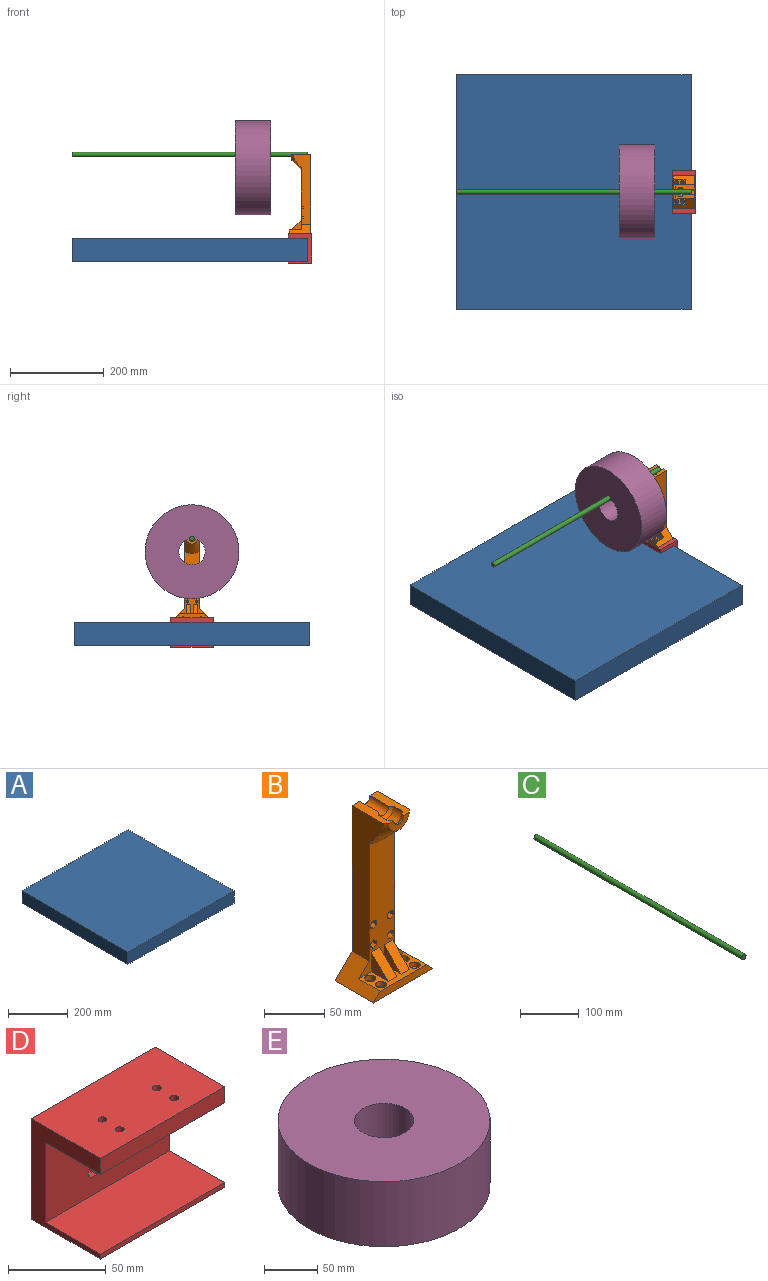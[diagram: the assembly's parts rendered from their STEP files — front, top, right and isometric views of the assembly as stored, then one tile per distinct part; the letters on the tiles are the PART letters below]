
ASSEMBLY  parts=5 mates=4
PART A: 6 faces, bbox 500x500x50 mm
  f0: plane 500x50mm, normal (0,-1,0), area 25000mm2, adj f1,f3,f4,f5
  f1: plane 500x50mm, normal (1,0,0), area 25000mm2, adj f0,f2,f4,f5
  f2: plane 500x50mm, normal (0,1,0), area 25000mm2, adj f1,f3,f4,f5
  f3: plane 500x50mm, normal (-1,0,0), area 25000mm2, adj f0,f2,f4,f5
  f4: plane 500x500mm, normal (0,0,1), area 250000mm2, adj f0,f1,f2,f3
  f5: plane 500x500mm, normal (0,0,-1), area 250000mm2, adj f0,f1,f2,f3
PART B: 68 faces, bbox 70x45x168 mm
  f0: plane 70x45mm, normal (0,0,-1), area 3085.5mm2, adj f11,f14,f17,f20,f64,f65,f66,f67
  f1: cone r=9mm half-angle=45deg, axis (0,-1,0), area 100mm2, adj f2,f53,f54,f55
  f2: cylinder r=9mm len=18mm, axis (0,1,0), area 282.7mm2, adj f1,f3,f53,f55
  f3: cone r=9mm half-angle=45deg, axis (0,1,0), area 100mm2, adj f2,f4,f53,f55
  f4: cylinder r=6mm len=12mm, axis (0,-1,0), area 37.7mm2, adj f3,f5,f53,f55
  f5: plane 24x12mm, normal (0,-1,0), area 169.6mm2, adj f4,f52,f53,f55
  f6: plane 8.33x7.21mm, normal (0,-1,0), area 28.9mm2, adj f22,f23,f24,f25,f26,f27,f56
  f7: plane 8.33x7.21mm, normal (0,-1,0), area 28.9mm2, adj f28,f29,f30,f31,f32,f33,f57
  f8: plane 8.33x7.21mm, normal (0,-1,0), area 28.9mm2, adj f34,f35,f36,f37,f38,f39,f58
  f9: plane 8.33x7.21mm, normal (0,-1,0), area 28.9mm2, adj f40,f41,f42,f43,f44,f45,f59
  f10: plane 9x9mm, normal (0,0,1), area 47.5mm2, adj f11,f12
  f11: cylinder r=2.27mm len=4.53mm, axis (0,0,-1), area 42.7mm2, adj f0,f10
  f12: cylinder r=4.5mm len=9mm, axis (0,0,1), area 141.4mm2, adj f10,f61
  f13: plane 9x9mm, normal (0,0,1), area 47.5mm2, adj f14,f15
  f14: cylinder r=2.27mm len=4.53mm, axis (0,0,-1), area 42.7mm2, adj f0,f13
  f15: cylinder r=4.5mm len=9mm, axis (0,0,1), area 141.4mm2, adj f13,f61
  f16: plane 9x9mm, normal (0,0,1), area 47.5mm2, adj f17,f18
  f17: cylinder r=2.27mm len=4.53mm, axis (0,0,-1), area 42.7mm2, adj f0,f16
  f18: cylinder r=4.5mm len=9mm, axis (0,0,1), area 141.4mm2, adj f16,f61
  f19: plane 9x9mm, normal (0,0,1), area 47.5mm2, adj f20,f21
  f20: cylinder r=2.27mm len=4.53mm, axis (0,0,-1), area 42.7mm2, adj f0,f19
  f21: cylinder r=4.5mm len=9mm, axis (0,0,1), area 141.4mm2, adj f19,f61
  f22: plane 4.8x3.61mm, normal (0.5,0,-0.87), area 20mm2, adj f6,f23,f27,f62
  f23: plane 4.8x4.16mm, normal (1,0,0), area 20mm2, adj f6,f22,f24,f62
  f24: plane 4.8x3.61mm, normal (0.5,0,0.87), area 20mm2, adj f6,f23,f25,f62
  f25: plane 4.8x3.61mm, normal (-0.5,0,0.87), area 20mm2, adj f6,f24,f26,f62
  f26: plane 4.8x4.16mm, normal (-1,0,0), area 20mm2, adj f6,f25,f27,f62
  f27: plane 4.8x3.61mm, normal (-0.5,0,-0.87), area 20mm2, adj f6,f22,f26,f62
  f28: plane 4.8x3.61mm, normal (0.5,0,-0.87), area 20mm2, adj f7,f29,f33,f62
  f29: plane 4.8x4.16mm, normal (1,0,0), area 20mm2, adj f7,f28,f30,f62
  f30: plane 4.8x3.61mm, normal (0.5,0,0.87), area 20mm2, adj f7,f29,f31,f62
  f31: plane 4.8x3.61mm, normal (-0.5,0,0.87), area 20mm2, adj f7,f30,f32,f62
  f32: plane 4.8x4.16mm, normal (-1,0,0), area 20mm2, adj f7,f31,f33,f62
  f33: plane 4.8x3.61mm, normal (-0.5,0,-0.87), area 20mm2, adj f7,f28,f32,f62
  f34: plane 4.8x3.61mm, normal (0.5,0,-0.87), area 20mm2, adj f8,f35,f39,f62
  f35: plane 4.8x4.16mm, normal (1,0,0), area 20mm2, adj f8,f34,f36,f62
  f36: plane 4.8x3.61mm, normal (0.5,0,0.87), area 20mm2, adj f8,f35,f37,f62
  f37: plane 4.8x3.61mm, normal (-0.5,0,0.87), area 20mm2, adj f8,f36,f38,f62
  f38: plane 4.8x4.16mm, normal (-1,0,0), area 20mm2, adj f8,f37,f39,f62
  f39: plane 4.8x3.61mm, normal (-0.5,0,-0.87), area 20mm2, adj f8,f34,f38,f62
  f40: plane 4.8x3.61mm, normal (0.5,0,-0.87), area 20mm2, adj f9,f41,f45,f62
  f41: plane 4.8x4.16mm, normal (1,0,0), area 20mm2, adj f9,f40,f42,f62
  f42: plane 4.8x3.61mm, normal (0.5,0,0.87), area 20mm2, adj f9,f41,f43,f62
  f43: plane 4.8x3.61mm, normal (-0.5,0,0.87), area 20mm2, adj f9,f42,f44,f62
  f44: plane 4.8x4.16mm, normal (-1,0,0), area 20mm2, adj f9,f43,f45,f62
  f45: plane 4.8x3.61mm, normal (-0.5,0,-0.87), area 20mm2, adj f9,f40,f44,f62
  f46: plane 20x20mm, normal (1,0,0), area 200mm2, adj f47,f61,f62
  f47: plane 20x20mm, normal (0,-0.71,0.71), area 282.8mm2, adj f46,f48,f61,f62
  f48: plane 20x20mm, normal (-1,0,0), area 200mm2, adj f47,f61,f62
  f49: plane 20x20mm, normal (1,0,0), area 200mm2, adj f50,f61,f62
  f50: plane 20x20mm, normal (0,-0.71,0.71), area 282.8mm2, adj f49,f51,f61,f62
  f51: plane 20x20mm, normal (-1,0,0), area 200mm2, adj f50,f61,f62
  f52: cone r=12mm half-angle=45deg, axis (0,1,0), area 986.3mm2, adj f5,f53,f55,f60,f62,f63
  f53: plane 40x9mm, normal (0,0,1), area 316.5mm2, adj f1,f2,f3,f4,f5,f52,f54,f63
  f54: cylinder r=6mm len=22mm, axis (0,-1,0), area 414.7mm2, adj f1,f53,f55,f67
  f55: plane 40x9mm, normal (0,0,1), area 316.5mm2, adj f1,f2,f3,f4,f5,f52,f54,f60
  f56: cylinder r=2.27mm len=15.2mm, axis (0,-1,0), area 216.4mm2, adj f6,f67
  f57: cylinder r=2.27mm len=15.2mm, axis (0,-1,0), area 216.4mm2, adj f7,f67
  f58: cylinder r=2.27mm len=15.2mm, axis (0,-1,0), area 216.4mm2, adj f8,f67
  f59: cylinder r=2.27mm len=15.2mm, axis (0,-1,0), area 216.4mm2, adj f9,f67
  f60: plane 148.01x37.01mm, normal (-1,0,0), area 3255.8mm2, adj f52,f55,f62,f64,f67
  f61: plane 54x25mm, normal (0,0,1), area 695.5mm2, adj f12,f15,f18,f21,f46,f47,f48,f49
  f62: plane 131.73x54mm, normal (0,-1,0), area 3440.3mm2, adj f22,f23,f24,f25,f26,f27,f28,f29
  f63: plane 148.01x37.01mm, normal (1,0,0), area 3255.8mm2, adj f52,f53,f62,f65,f67
  f64: plane 45x20mm, normal (-0.71,0,0.71), area 848.5mm2, adj f0,f60,f61,f62,f66,f67
  f65: plane 45x20mm, normal (0.71,0,0.71), area 848.5mm2, adj f0,f61,f62,f63,f66,f67
  f66: plane 70x8mm, normal (0,-1,0), area 496mm2, adj f0,f61,f64,f65
  f67: plane 168x70mm, normal (0,1,0), area 5318.9mm2, adj f0,f53,f54,f55,f56,f57,f58,f59
PART C: 3 faces, bbox 10x500x10 mm
  f0: cylinder r=5mm len=500mm, axis (0,1,0), area 15708mm2, adj f1,f2
  f1: plane 10x10mm, normal (0,-1,0), area 78.5mm2, adj f0
  f2: plane 10x10mm, normal (0,1,0), area 78.5mm2, adj f0
PART D: 78 faces, bbox 90x50x63.1 mm
  f0: cylinder r=2.27mm len=4.8mm, axis (0,0,-1), area 68.3mm2, adj f8,f67
  f1: cylinder r=2.27mm len=4.8mm, axis (0,0,-1), area 68.3mm2, adj f8,f60
  f2: cylinder r=2.27mm len=4.8mm, axis (0,0,-1), area 68.3mm2, adj f8,f53
  f3: cylinder r=2.27mm len=4.8mm, axis (0,0,-1), area 68.3mm2, adj f8,f46
  f4: cylinder r=2.27mm len=4.53mm, axis (0,-1,0), area 45.6mm2, adj f39,f75
  f5: cylinder r=2.27mm len=4.53mm, axis (0,-1,0), area 45.6mm2, adj f32,f74
  f6: cylinder r=2.27mm len=4.53mm, axis (0,-1,0), area 45.6mm2, adj f25,f77
  f7: cylinder r=2.27mm len=4.53mm, axis (0,-1,0), area 45.6mm2, adj f18,f76
  f8: plane 90x50mm, normal (0,0,1), area 4435.5mm2, adj f0,f1,f2,f3,f10,f12,f13,f15
  f9: plane 90x50.1mm, normal (0,-1,0), area 4328.9mm2, adj f10,f12,f14,f16,f19,f20,f21,f22
  f10: plane 63.1x50mm, normal (-1,0,0), area 1151mm2, adj f8,f9,f11,f13,f14,f15,f16,f17
  f11: plane 90x50mm, normal (0,0,-1), area 4500mm2, adj f10,f12,f13,f17
  f12: plane 63.1x50mm, normal (1,0,0), area 1151mm2, adj f8,f9,f11,f13,f14,f15,f16,f17
  f13: plane 90x63.1mm, normal (0,1,0), area 5450.3mm2, adj f8,f10,f11,f12,f74,f75,f76,f77
  f14: plane 90x40mm, normal (0,0,-1), area 3419.9mm2, adj f9,f10,f12,f15,f47,f48,f49,f50
  f15: plane 90x10mm, normal (0,-1,0), area 900mm2, adj f8,f10,f12,f14
  f16: plane 90x40mm, normal (0,0,1), area 3600mm2, adj f9,f10,f12,f17
  f17: plane 90x3mm, normal (0,-1,0), area 270mm2, adj f10,f11,f12,f16
  f18: plane 8.33x7.21mm, normal (0,-1,0), area 28.9mm2, adj f7,f19,f20,f21,f22,f23,f24
  f19: plane 4.8x3.61mm, normal (-0.87,0,0.5), area 20mm2, adj f9,f18,f20,f24
  f20: plane 4.8x3.61mm, normal (-0.87,0,-0.5), area 20mm2, adj f9,f18,f19,f21
  f21: plane 4.8x4.16mm, normal (0,0,-1), area 20mm2, adj f9,f18,f20,f22
  f22: plane 4.8x3.61mm, normal (0.87,0,-0.5), area 20mm2, adj f9,f18,f21,f23
  f23: plane 4.8x3.61mm, normal (0.87,0,0.5), area 20mm2, adj f9,f18,f22,f24
  f24: plane 4.8x4.16mm, normal (0,0,1), area 20mm2, adj f9,f18,f19,f23
  f25: plane 8.33x7.21mm, normal (0,-1,0), area 28.9mm2, adj f6,f26,f27,f28,f29,f30,f31
  f26: plane 4.8x3.61mm, normal (-0.87,0,0.5), area 20mm2, adj f9,f25,f27,f31
  f27: plane 4.8x3.61mm, normal (-0.87,0,-0.5), area 20mm2, adj f9,f25,f26,f28
  f28: plane 4.8x4.16mm, normal (0,0,-1), area 20mm2, adj f9,f25,f27,f29
  f29: plane 4.8x3.61mm, normal (0.87,0,-0.5), area 20mm2, adj f9,f25,f28,f30
  f30: plane 4.8x3.61mm, normal (0.87,0,0.5), area 20mm2, adj f9,f25,f29,f31
  f31: plane 4.8x4.16mm, normal (0,0,1), area 20mm2, adj f9,f25,f26,f30
  f32: plane 8.33x7.21mm, normal (0,-1,0), area 28.9mm2, adj f5,f33,f34,f35,f36,f37,f38
  f33: plane 4.8x3.61mm, normal (-0.87,0,0.5), area 20mm2, adj f9,f32,f34,f38
  f34: plane 4.8x3.61mm, normal (-0.87,0,-0.5), area 20mm2, adj f9,f32,f33,f35
  f35: plane 4.8x4.16mm, normal (0,0,-1), area 20mm2, adj f9,f32,f34,f36
  f36: plane 4.8x3.61mm, normal (0.87,0,-0.5), area 20mm2, adj f9,f32,f35,f37
  f37: plane 4.8x3.61mm, normal (0.87,0,0.5), area 20mm2, adj f9,f32,f36,f38
  f38: plane 4.8x4.16mm, normal (0,0,1), area 20mm2, adj f9,f32,f33,f37
  f39: plane 8.33x7.21mm, normal (0,-1,0), area 28.9mm2, adj f4,f40,f41,f42,f43,f44,f45
  f40: plane 4.8x3.61mm, normal (-0.87,0,0.5), area 20mm2, adj f9,f39,f41,f45
  f41: plane 4.8x3.61mm, normal (-0.87,0,-0.5), area 20mm2, adj f9,f39,f40,f42
  f42: plane 4.8x4.16mm, normal (0,0,-1), area 20mm2, adj f9,f39,f41,f43
  f43: plane 4.8x3.61mm, normal (0.87,0,-0.5), area 20mm2, adj f9,f39,f42,f44
  f44: plane 4.8x3.61mm, normal (0.87,0,0.5), area 20mm2, adj f9,f39,f43,f45
  f45: plane 4.8x4.16mm, normal (0,0,1), area 20mm2, adj f9,f39,f40,f44
  f46: plane 8.33x7.21mm, normal (0,0,-1), area 28.9mm2, adj f3,f47,f48,f49,f50,f51,f52
  f47: plane 5.2x3.61mm, normal (-0.87,-0.5,0), area 21.6mm2, adj f14,f46,f48,f52
  f48: plane 5.2x3.61mm, normal (-0.87,0.5,0), area 21.6mm2, adj f14,f46,f47,f49
  f49: plane 5.2x4.16mm, normal (0,1,0), area 21.6mm2, adj f14,f46,f48,f50
  f50: plane 5.2x3.61mm, normal (0.87,0.5,0), area 21.6mm2, adj f14,f46,f49,f51
  f51: plane 5.2x3.61mm, normal (0.87,-0.5,0), area 21.6mm2, adj f14,f46,f50,f52
  f52: plane 5.2x4.16mm, normal (0,-1,0), area 21.6mm2, adj f14,f46,f47,f51
  f53: plane 8.33x7.21mm, normal (0,0,-1), area 28.9mm2, adj f2,f54,f55,f56,f57,f58,f59
  f54: plane 5.2x3.61mm, normal (-0.87,-0.5,0), area 21.6mm2, adj f14,f53,f55,f59
  f55: plane 5.2x3.61mm, normal (-0.87,0.5,0), area 21.6mm2, adj f14,f53,f54,f56
  f56: plane 5.2x4.16mm, normal (0,1,0), area 21.6mm2, adj f14,f53,f55,f57
  f57: plane 5.2x3.61mm, normal (0.87,0.5,0), area 21.6mm2, adj f14,f53,f56,f58
  f58: plane 5.2x3.61mm, normal (0.87,-0.5,0), area 21.6mm2, adj f14,f53,f57,f59
  f59: plane 5.2x4.16mm, normal (0,-1,0), area 21.6mm2, adj f14,f53,f54,f58
  f60: plane 8.33x7.21mm, normal (0,0,-1), area 28.9mm2, adj f1,f61,f62,f63,f64,f65,f66
  f61: plane 5.2x3.61mm, normal (-0.87,-0.5,0), area 21.6mm2, adj f14,f60,f62,f66
  f62: plane 5.2x3.61mm, normal (-0.87,0.5,0), area 21.6mm2, adj f14,f60,f61,f63
  f63: plane 5.2x4.16mm, normal (0,1,0), area 21.6mm2, adj f14,f60,f62,f64
  f64: plane 5.2x3.61mm, normal (0.87,0.5,0), area 21.6mm2, adj f14,f60,f63,f65
  f65: plane 5.2x3.61mm, normal (0.87,-0.5,0), area 21.6mm2, adj f14,f60,f64,f66
  f66: plane 5.2x4.16mm, normal (0,-1,0), area 21.6mm2, adj f14,f60,f61,f65
  f67: plane 8.33x7.21mm, normal (0,0,-1), area 28.9mm2, adj f0,f68,f69,f70,f71,f72,f73
  f68: plane 5.2x3.61mm, normal (-0.87,-0.5,0), area 21.6mm2, adj f14,f67,f69,f73
  f69: plane 5.2x3.61mm, normal (-0.87,0.5,0), area 21.6mm2, adj f14,f67,f68,f70
  f70: plane 5.2x4.16mm, normal (0,1,0), area 21.6mm2, adj f14,f67,f69,f71
  f71: plane 5.2x3.61mm, normal (0.87,0.5,0), area 21.6mm2, adj f14,f67,f70,f72
  f72: plane 5.2x3.61mm, normal (0.87,-0.5,0), area 21.6mm2, adj f14,f67,f71,f73
  f73: plane 5.2x4.16mm, normal (0,-1,0), area 21.6mm2, adj f14,f67,f68,f72
  f74: cone r=4.27mm half-angle=45deg, axis (0,1,0), area 58mm2, adj f5,f13
  f75: cone r=4.27mm half-angle=45deg, axis (0,1,0), area 58mm2, adj f4,f13
  f76: cone r=4.27mm half-angle=45deg, axis (0,1,0), area 58mm2, adj f7,f13
  f77: cone r=4.27mm half-angle=45deg, axis (0,1,0), area 58mm2, adj f6,f13
PART E: 4 faces, bbox 200x200x75 mm
  f0: cylinder r=28mm len=75mm, axis (0,0,-1), area 13194.7mm2, adj f2,f3
  f1: cylinder r=100mm len=200mm, axis (0,0,-1), area 47123.9mm2, adj f2,f3
  f2: plane 200x200mm, normal (0,0,1), area 28952.9mm2, adj f0,f1
  f3: plane 200x200mm, normal (0,0,-1), area 28952.9mm2, adj f0,f1
PLACE A t=(394.91,26.05,98.67)mm
PLACE B rot(axis=(0,0,-1),90deg) t=(652.31,26.05,123.72)mm
PLACE C rot(axis=(0,0,-1),90deg) t=(394.91,26.05,301.72)mm
PLACE D rot(axis=(0,0,-1),90deg) t=(654.91,26.05,123.72)mm
PLACE E rot(axis=(-0.58,-0.58,0.58),120deg) t=(530.02,26.05,273.72)mm
MATE fastened B.f0 <-> D.f8  axis (0,0,-1) through (630.02,26.05,133.72)mm
MATE slider E.f3 <-> C.f0  axis (-1,0,0) through (567.52,26.05,301.72)mm
MATE planar C.f0 <-> A.f1  axis (1,0,0) through (644.91,26.05,301.72)mm
MATE fastened D.f9 <-> A.f1  axis (-1,0,0) through (644.91,26.05,98.67)mm
